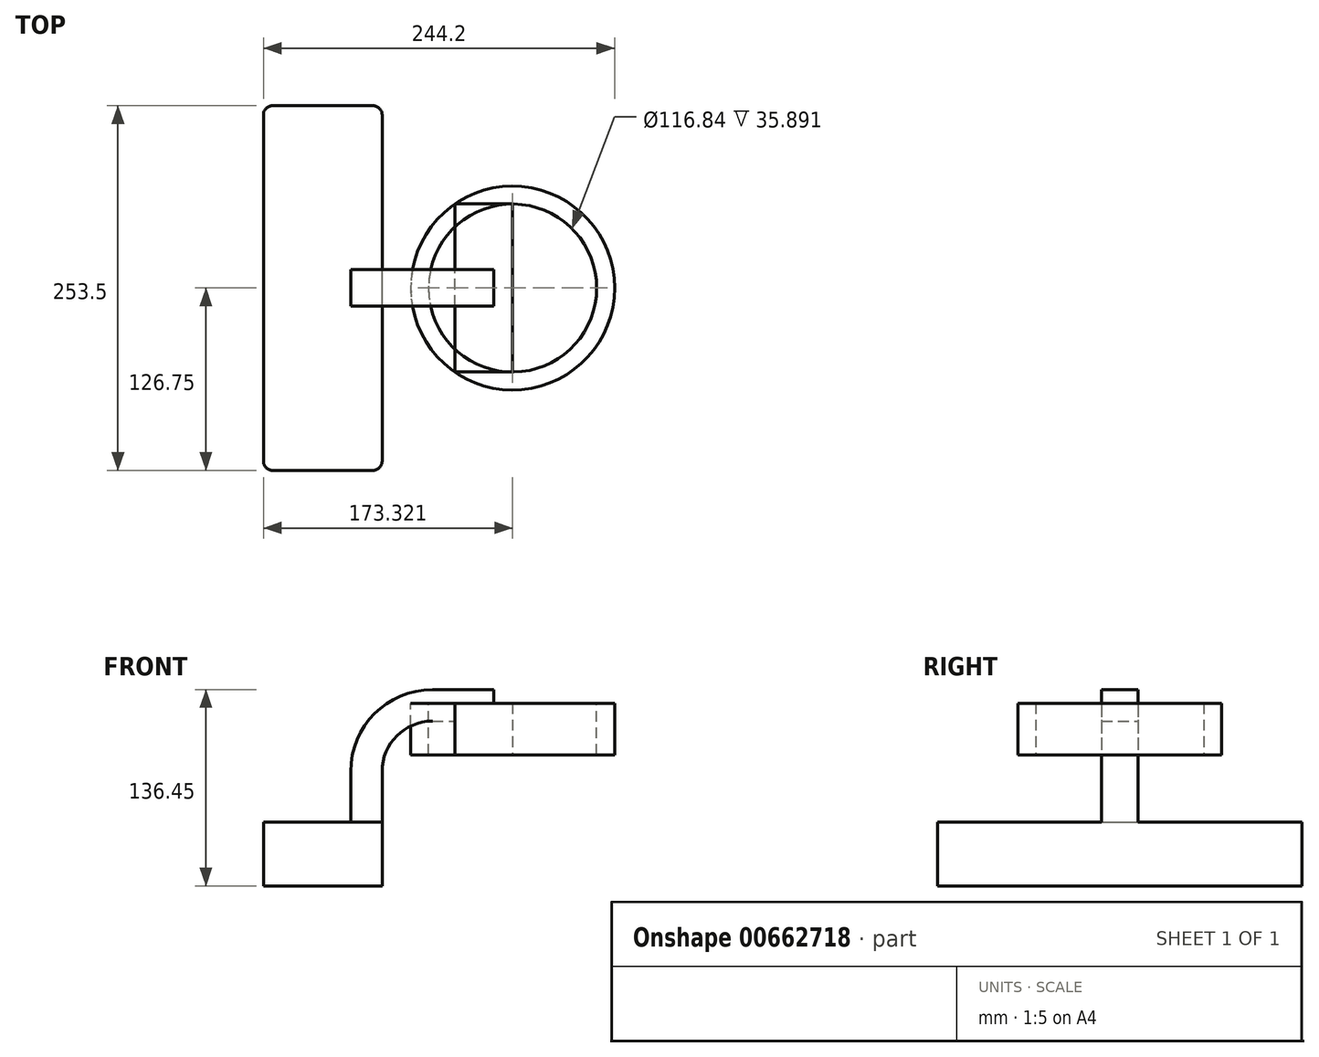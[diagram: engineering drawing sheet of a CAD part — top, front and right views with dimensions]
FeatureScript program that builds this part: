
annotation { "Feature Type Name" : "Feature", "Feature Type Description" : "" }
export const myFeature = defineFeature(function(context is Context, id is Id, definition is map)
    precondition{}
    {
        {
            var Q0;
            Q0=qCreatedBy(makeId("Front.planeOp"),FACE);
            var sketch = newSketch(context, id + "F0", { "sketchPlane" : qUnion([Q0])});
            skLineSegment(sketch, "E0.bottom", {"start": v(-41.5, 12.5) * mm, "end": v(41.06, 12.5) * mm});
            skLineSegment(sketch, "E0.top", {"start": v(-41.5, -31.95) * mm, "end": v(41.06, -31.95) * mm});
            skLineSegment(sketch, "E0.left", {"start": v(-41.5, 12.5) * mm, "end": v(-41.5, -31.95) * mm});
            skLineSegment(sketch, "E0.right", {"start": v(41.06, 12.5) * mm, "end": v(41.06, -31.95) * mm});
            skLineSegment(sketch, "E1.bottom", {"start": v(91.7, 95.12) * mm, "end": v(131.83, 95.12) * mm});
            skLineSegment(sketch, "E1.top", {"start": v(91.7, 59.23) * mm, "end": v(131.83, 59.23) * mm});
            skLineSegment(sketch, "E1.left", {"start": v(91.7, 95.12) * mm, "end": v(91.7, 59.23) * mm});
            skLineSegment(sketch, "E1.right", {"start": v(131.83, 95.12) * mm, "end": v(131.83, 59.23) * mm});
            skLineSegment(sketch, "E2", {"start": v(41.06, 12.5) * mm, "end": v(41.06, 47.7) * mm});
            skArc(sketch, "E3", {"start": v(41.06, 47.7) * mm, "mid": v(51.29, 72.4) * mm, "end": v(75.98, 82.63) * mm});
            skLineSegment(sketch, "E4", {"start": v(75.98, 82.63) * mm, "end": v(118.54, 82.63) * mm});
            skLineSegment(sketch, "E5.0", {"start": v(75.98, 104.5) * mm, "end": v(118.54, 104.5) * mm});
            skArc(sketch, "E5.1", {"start": v(19.2, 47.7) * mm, "mid": v(35.83, 87.86) * mm, "end": v(75.98, 104.5) * mm});
            skLineSegment(sketch, "E5.2", {"start": v(19.2, 18.52) * mm, "end": v(19.2, 47.7) * mm});
            skLineSegment(sketch, "E6", {"start": v(118.54, 104.5) * mm, "end": v(118.54, 82.63) * mm});
            skFitSpline(sketch, "E7", {"points": [v(-41.5, 12.5) * mm, v(75.98, 104.5) * mm], "startDerivative": vector(9.82, 137.08) * mm, "endDerivative": vector(125, -57.42) * mm});
            skLineSegment(sketch, "E8", {"start": v(19.2, 18.52) * mm, "end": v(19.2, 12.5) * mm});
            skSolve(sketch);
        }
        {
            var Q0;
            Q0=makeQuery(id+"F0.imprint","IMPRINT",FACE,{"disambiguationData":[TD([[makeQuery(id+"F0.imprint","IMPRINT",EDGE,{"derivedFrom":sQuery(id+"F0.wireOp",EDGE,"E0.top")}),1.0]])]});
            extrude(context, id + "F1", {"entities" : qUnion([Q0]), "endBound" : BoundingType.SYMMETRIC, "depth" : 253.5 * mm, "offsetDistance" : 25.4 * mm});
        }
        {
            var Q0;
            {var subQ8=sQuery(id+"F0.wireOp",EDGE,"E2");Q0=makeQuery(id+"F0.imprint","IMPRINT",FACE,{"disambiguationData":[TD([[makeQuery(id+"F0.imprint","IMPRINT",EDGE,{"derivedFrom":subQ8}),1.0]])]});}
            extrude(context, id + "F2", {"entities" : qUnion([Q0]), "operationType" : NewBodyOperationType.ADD, "endBound" : BoundingType.SYMMETRIC, "depth" : 25.4 * mm, "offsetDistance" : 25.4 * mm});
        }
        {
            var Q0;
            {var subQ2=sQuery(id+"F0.wireOp",EDGE,"E1.top");Q0=makeQuery(id+"F0.imprint","IMPRINT",FACE,{"disambiguationData":[TD([[makeQuery(id+"F0.imprint","IMPRINT",EDGE,{"derivedFrom":subQ2}),1.0]])]});}
            var Q1;
            {var subQ0=sQuery(id+"F0.wireOp",EDGE,"E1.left");var subQ1=sQuery(id+"F0.wireOp",EDGE,"E1.bottom");var subQ2=makeQuery(id+"F0.imprint","INTERSECT",VERTEX,{"derivedFrom":[subQ1,subQ0]});Q1=makeQuery(id+"F0.imprint","IMPRINT",FACE,{"disambiguationData":[TD([[makeQuery(id+"F0.imprint","IMPRINT",EDGE,{"disambiguationData":[TD([[subQ2,-1.0]])],"derivedFrom":subQ1}),-1.0]])]});}
            extrude(context, id + "F3", {"entities" : qUnion([Q0, Q1]), "operationType" : NewBodyOperationType.ADD, "endBound" : BoundingType.SYMMETRIC, "depth" : 116.84 * mm, "offsetDistance" : 25.4 * mm});
        }
        {
            var Q0;
            Q0=makeQuery(id+"F0.imprint","IMPRINT",FACE,{"disambiguationData":[TD([[makeQuery(id+"F0.imprint","IMPRINT",EDGE,{"derivedFrom":sQuery(id+"F0.wireOp",EDGE,"E5.1")}),1.0]])]});
            extrude(context, id + "F4", {"entities" : qUnion([Q0]), "operationType" : NewBodyOperationType.ADD, "endBound" : BoundingType.SYMMETRIC, "depth" : 2.54 * mm, "offsetDistance" : 25.4 * mm});
        }
        {
            var Q0;
            Q0=makeQuery(id+"F3.opExtrude","CAP_FACE",FACE,{"disambiguationData":[OSD([sQuery(id+"F0.wireOp",EDGE,"E1.bottom"),sQuery(id+"F0.wireOp",EDGE,"E1.top"),sQuery(id+"F0.wireOp",EDGE,"E1.left"),sQuery(id+"F0.wireOp",EDGE,"E1.right")])],"isStart":true});
            var Q1;
            Q1=sQuery(id+"F0.wireOp",EDGE,"E1.right");
            revolve(context, id + "F5", {"entities" : qUnion([Q0]), "axis" : qUnion([Q1]), "revolveType" : RevolveType.FULL});
        }
        {
            var Q0;
            Q0=makeQuery(id+"F1.opExtrude","CAP_EDGE",EDGE,{"disambiguationData":[OSD([sQuery(id+"F0.wireOp",EDGE,"E0.right")])],"isStart":true});
            var Q1;
            Q1=makeQuery(id+"F1.opExtrude","CAP_EDGE",EDGE,{"disambiguationData":[OSD([sQuery(id+"F0.wireOp",EDGE,"E0.right")])],"isStart":false});
            var Q2;
            Q2=makeQuery(id+"F1.opExtrude","CAP_EDGE",EDGE,{"disambiguationData":[OSD([sQuery(id+"F0.wireOp",EDGE,"E0.left")])],"isStart":false});
            var Q3;
            Q3=makeQuery(id+"F1.opExtrude","CAP_EDGE",EDGE,{"disambiguationData":[OSD([sQuery(id+"F0.wireOp",EDGE,"E0.left")])],"isStart":true});
            fillet(context, id + "F6", {"entities" : qUnion([Q0, Q1, Q2, Q3]), "radius" : 6.35 * mm, "tangentPropagation" : true, "allowEdgeOverflow" : false});
        }
    });
